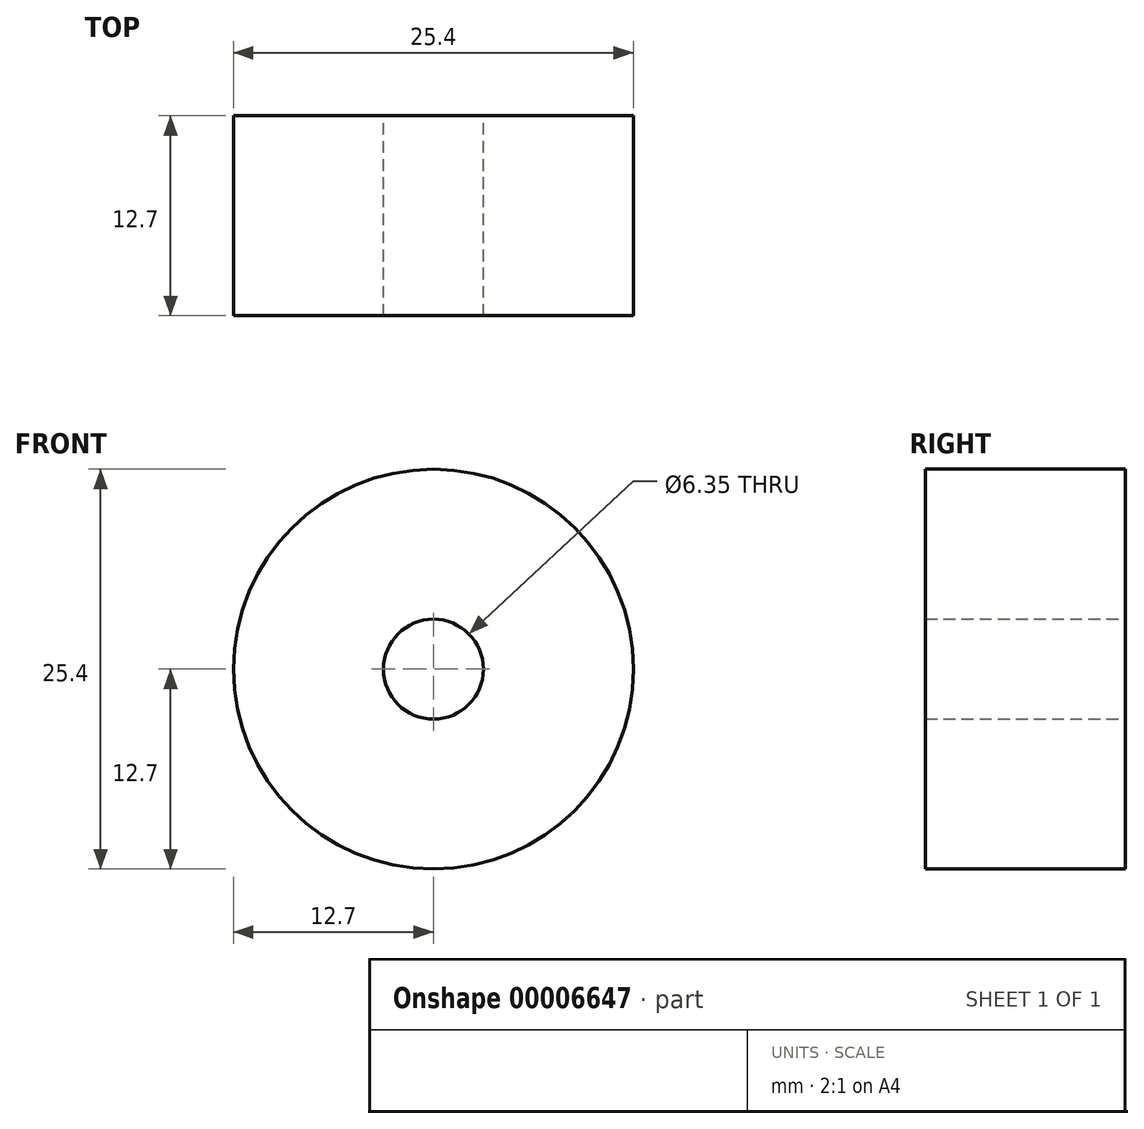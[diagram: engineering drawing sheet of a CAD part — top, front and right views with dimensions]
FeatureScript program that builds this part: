
annotation { "Feature Type Name" : "Feature", "Feature Type Description" : "" }
export const myFeature = defineFeature(function(context is Context, id is Id, definition is map)
    precondition{}
    {
        {
            var Q0;
            Q0=qCreatedBy(makeId("Front.planeOp"),FACE);
            var sketch = newSketch(context, id + "F0", { "sketchPlane" : qUnion([Q0])});
            skCircle(sketch, "E0", {"center": v(0, 0) * mm, "radius": 12.7 * mm});
            skCircle(sketch, "E1", {"center": v(0, 0) * mm, "radius": 3.18 * mm});
            skSolve(sketch);
        }
        {
            var Q0;
            Q0 = qSketchRegion(id + "F0", true);
            extrude(context, id + "F1", {"entities" : qUnion([Q0]), "depth" : 12.7 * mm});
        }
    });
